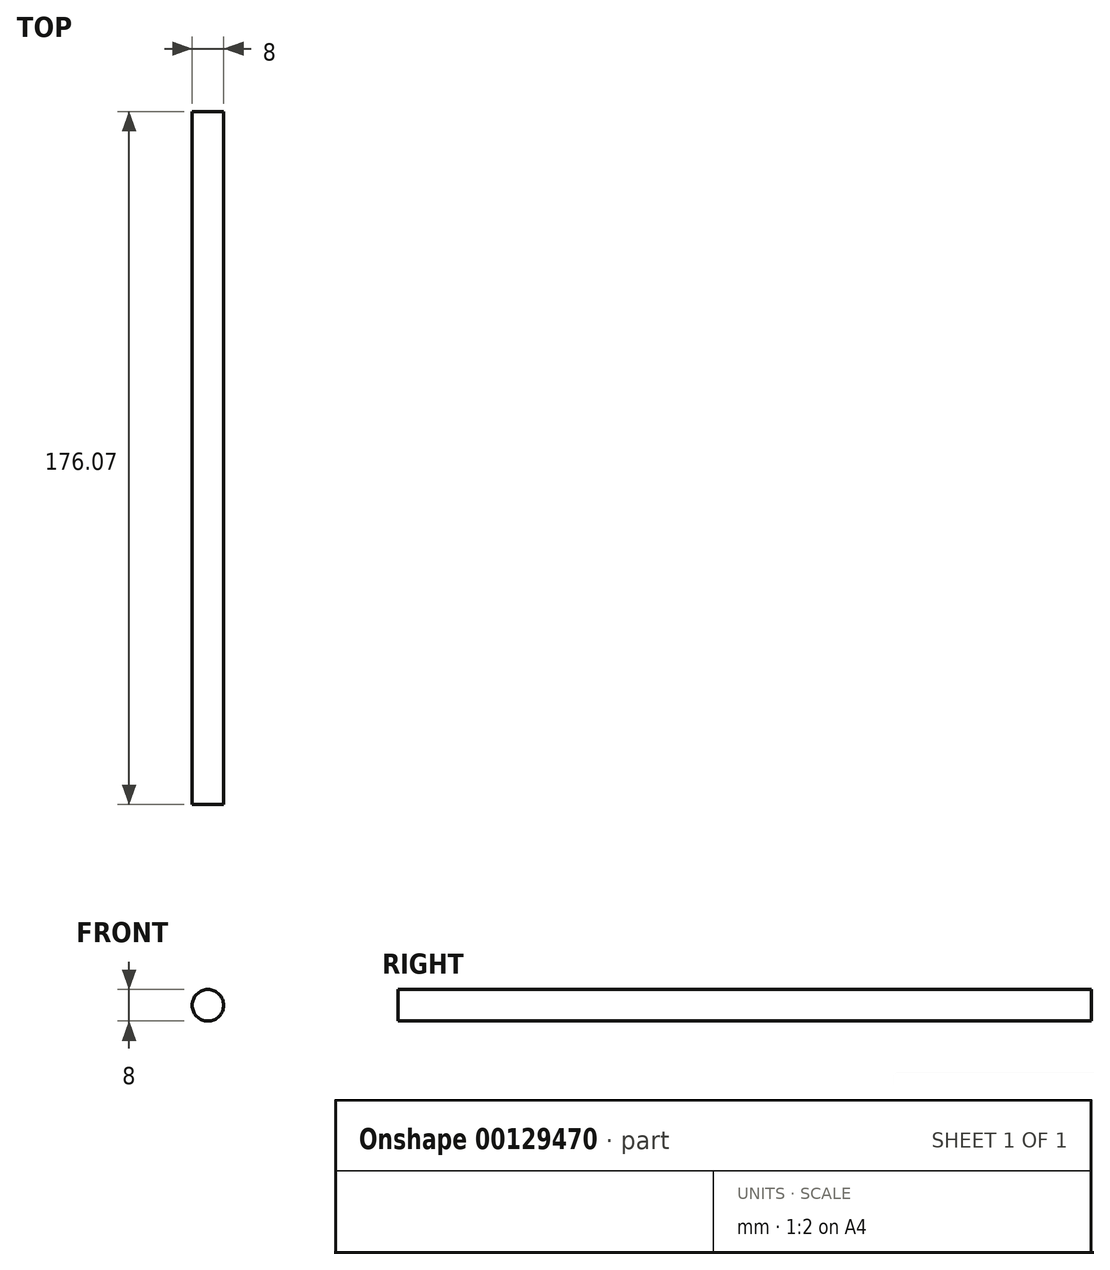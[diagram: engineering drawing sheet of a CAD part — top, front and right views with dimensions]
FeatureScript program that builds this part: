
annotation { "Feature Type Name" : "Feature", "Feature Type Description" : "" }
export const myFeature = defineFeature(function(context is Context, id is Id, definition is map)
    precondition{}
    {
        {
            var Q0;
            Q0=qCreatedBy(makeId("Front.planeOp"),FACE);
            var sketch = newSketch(context, id + "F0", { "sketchPlane" : qUnion([Q0])});
            skCircle(sketch, "E0", {"center": v(0, 0) * mm, "radius": 4 * mm});
            skSolve(sketch);
        }
        {
            var Q0;
            Q0=qSketchRegion(id+"F0",true);
            extrude(context, id + "F1", {"entities" : qUnion([Q0]), "depth" : 176.07 * mm});
        }
    });
